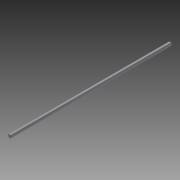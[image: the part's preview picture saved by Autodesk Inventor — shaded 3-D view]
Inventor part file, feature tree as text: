
AUTODESK INVENTOR PART (.ipt)
format: ipt  version: 2015 SP1 (Build 190203100, 203)  size: 76,800 bytes
history: native  units: in
note: dims shown in document units (in); Inventor stores cm internally (conversion verified against a paired STEP export)
features: extrude x1, sketch x1
ambient origin geometry x8: Origin, YZ Plane, XZ Plane, XY Plane, X Axis, Y Axis, Z Axis, Center Point
bodies: Solid1 (feature_tree)
feature tree (2):
  extrude  "Extrusion1"  Depth=0.4375in
  sketch  "Sketch1"  dims[d0=0.4375in d1=0.4375in d2=0.4375in d3=0.2188in d4=120.0deg d5=120.0deg d6=0.2188in d7=0.2188in d8=23.0in d9=0.0in]
